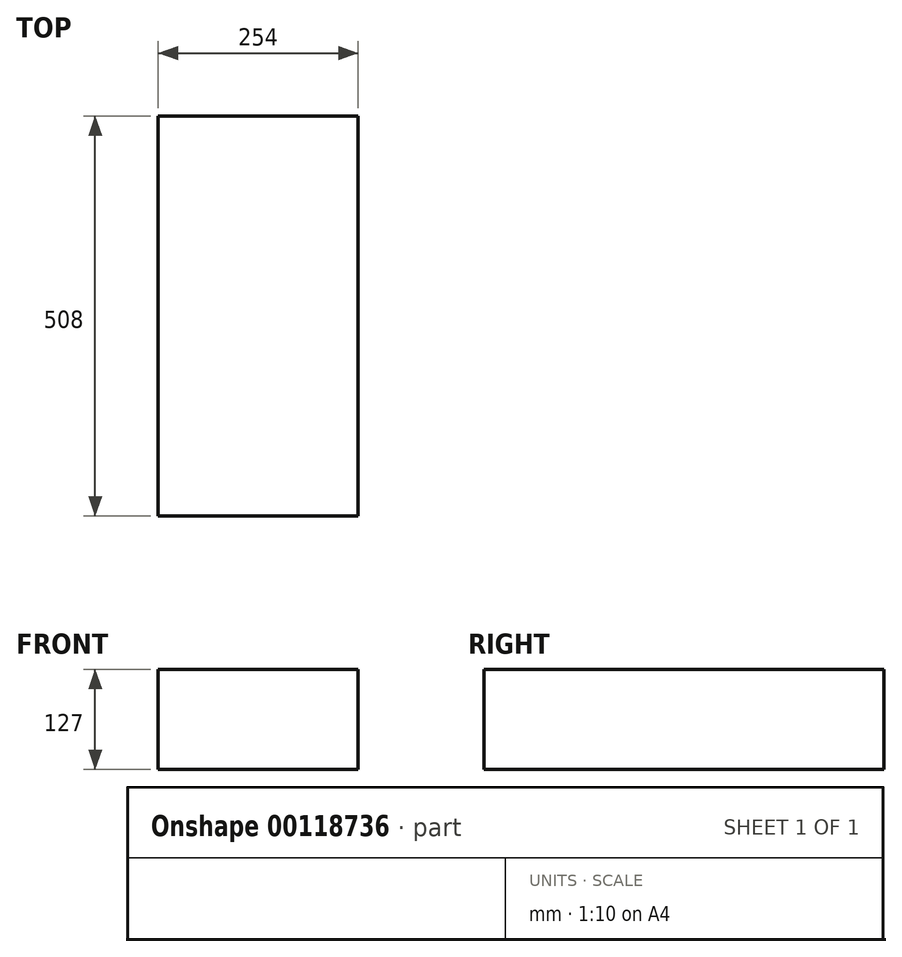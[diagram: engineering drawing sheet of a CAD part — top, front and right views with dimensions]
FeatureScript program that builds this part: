
annotation { "Feature Type Name" : "Feature", "Feature Type Description" : "" }
export const myFeature = defineFeature(function(context is Context, id is Id, definition is map)
    precondition{}
    {
        {
            var Q0;
            Q0=qCreatedBy(makeId("Top.planeOp"),FACE);
            var sketch = newSketch(context, id + "F1", { "sketchPlane" : qUnion([Q0])});
            skLineSegment(sketch, "E0.bottom", {"start": v(0, 0) * mm, "end": v(0, 0) * mm});
            skLineSegment(sketch, "E0.top", {"start": v(0, 0) * mm, "end": v(0, 0) * mm});
            skLineSegment(sketch, "E0.left", {"start": v(0, 0) * mm, "end": v(0, 0) * mm});
            skLineSegment(sketch, "E0.right", {"start": v(0, 0) * mm, "end": v(0, 0) * mm});
            skPoint(sketch, "E0.middle", {"position": v(0, 0) * mm});
            skLineSegment(sketch, "E1.bottom", {"start": v(127, 254) * mm, "end": v(-127, 254) * mm});
            skLineSegment(sketch, "E1.top", {"start": v(127, -254) * mm, "end": v(-127, -254) * mm});
            skLineSegment(sketch, "E1.left", {"start": v(127, 254) * mm, "end": v(127, -254) * mm});
            skLineSegment(sketch, "E1.right", {"start": v(-127, 254) * mm, "end": v(-127, -254) * mm});
            skSolve(sketch);
        }
        {
            var Q0;
            Q0 = qSketchRegion(id + "F1", true);
            extrude(context, id + "F2", {"entities" : qUnion([Q0]), "depth" : 127 * mm});
        }
    });
